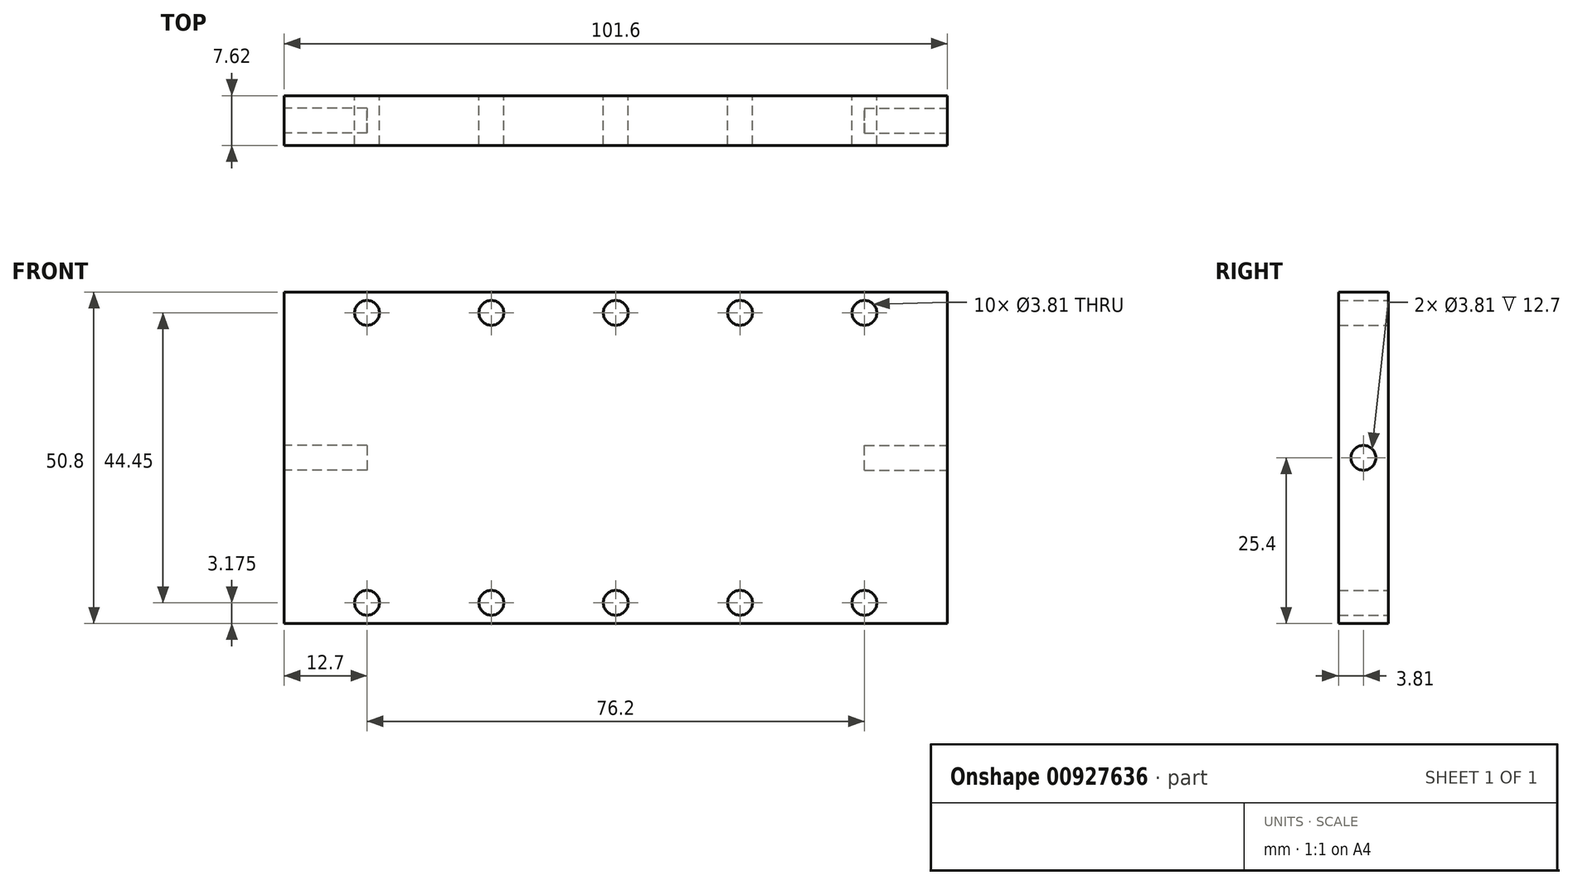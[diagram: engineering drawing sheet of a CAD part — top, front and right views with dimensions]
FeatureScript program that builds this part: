
annotation { "Feature Type Name" : "Feature", "Feature Type Description" : "" }
export const myFeature = defineFeature(function(context is Context, id is Id, definition is map)
    precondition{}
    {
        {
            var Q0;
            Q0=qCreatedBy(makeId("Front.planeOp"),FACE);
            var sketch = newSketch(context, id + "F0", { "sketchPlane" : qUnion([Q0])});
            skLineSegment(sketch, "E0.bottom", {"start": v(-50.8, 25.4) * mm, "end": v(50.8, 25.4) * mm});
            skLineSegment(sketch, "E0.top", {"start": v(-50.8, -25.4) * mm, "end": v(50.8, -25.4) * mm});
            skLineSegment(sketch, "E0.left", {"start": v(-50.8, 25.4) * mm, "end": v(-50.8, -25.4) * mm});
            skLineSegment(sketch, "E0.right", {"start": v(50.8, 25.4) * mm, "end": v(50.8, -25.4) * mm});
            skPoint(sketch, "E0.middle", {"position": v(0, 0) * mm});
            skCircle(sketch, "E1", {"center": v(-38.1, 22.23) * mm, "radius": 1.9 * mm});
            skCircle(sketch, "E2.1.0.0", {"center": v(-19.05, 22.23) * mm, "radius": 1.9 * mm});
            skCircle(sketch, "E2.2.0.0", {"center": v(0, 22.23) * mm, "radius": 1.9 * mm});
            skCircle(sketch, "E2.3.0.0", {"center": v(19.05, 22.23) * mm, "radius": 1.9 * mm});
            skCircle(sketch, "E2.4.0.0", {"center": v(38.1, 22.23) * mm, "radius": 1.9 * mm});
            skLineSegment(sketch, "E2.direction1", {"start": v(-38.1, 22.23) * mm, "end": v(-19.05, 22.23) * mm, "construction": true});
            skCircle(sketch, "E3.MirrorC", {"center": v(-38.1, -22.23) * mm, "radius": 1.9 * mm});
            skCircle(sketch, "E4.MirrorC", {"center": v(-19.05, -22.23) * mm, "radius": 1.9 * mm});
            skCircle(sketch, "E5.MirrorC", {"center": v(19.05, -22.23) * mm, "radius": 1.9 * mm});
            skCircle(sketch, "E6.MirrorC", {"center": v(38.1, -22.23) * mm, "radius": 1.9 * mm});
            skCircle(sketch, "E7.MirrorC", {"center": v(0, -22.23) * mm, "radius": 1.9 * mm});
            skSolve(sketch);
        }
        {
            var Q0;
            Q0=makeQuery(id+"F0.imprint","IMPRINT",FACE,{"disambiguationData":[TD([[makeQuery(id+"F0.imprint","IMPRINT",EDGE,{"derivedFrom":sQuery(id+"F0.wireOp",EDGE,"E0.bottom")}),-1.0]])]});
            extrude(context, id + "F1", {"entities" : qUnion([Q0]), "endBound" : BoundingType.SYMMETRIC, "depth" : 7.62 * mm, "offsetDistance" : 25.4 * mm});
        }
        {
            var Q0;
            Q0=makeQuery(id+"F1.opExtrude","SWEPT_FACE",FACE,{"disambiguationData":[OSD([sQuery(id+"F0.wireOp",EDGE,"E0.right")])]});
            cPlane(context, id + "F2", {"entities" : qUnion([Q0]), "cplaneType" : CPlaneType.OFFSET, "offset" : 0 * mm, "width" : 152.4 * mm, "height" : 152.4 * mm});
        }
        {
            var Q0;
            Q0=qCreatedBy(id+"F2.planeOp",FACE);
            var sketch = newSketch(context, id + "F3", { "sketchPlane" : qUnion([Q0])});
            skCircle(sketch, "E8", {"center": v(0, 0) * mm, "radius": 1.9 * mm});
            skLineSegment(sketch, "E9.bottom", {"start": v(3.81, -25.4) * mm, "end": v(-3.8, -25.4) * mm});
            skLineSegment(sketch, "E9.top", {"start": v(3.8, 25.4) * mm, "end": v(-3.81, 25.4) * mm});
            skLineSegment(sketch, "E9.left", {"start": v(3.81, -25.4) * mm, "end": v(3.8, 25.4) * mm});
            skLineSegment(sketch, "E9.right", {"start": v(-3.8, -25.4) * mm, "end": v(-3.81, 25.4) * mm});
            skSolve(sketch);
        }
        {
            var Q0;
            Q0=makeQuery(id+"F3.imprint","IMPRINT",FACE,{"disambiguationData":[TD([[makeQuery(id+"F3.imprint","IMPRINT",EDGE,{"derivedFrom":sQuery(id+"F3.wireOp",EDGE,"E8")}),1.0]])]});
            extrude(context, id + "F4", {"entities" : qUnion([Q0]), "operationType" : NewBodyOperationType.REMOVE, "oppositeDirection" : true, "depth" : 12.7 * mm, "offsetDistance" : 25.4 * mm});
        }
        {
            var Q0;
            Q0=makeQuery(id+"F1.opExtrude","SWEPT_FACE",FACE,{"disambiguationData":[OSD([sQuery(id+"F0.wireOp",EDGE,"E0.left")])]});
            cPlane(context, id + "F5", {"entities" : qUnion([Q0]), "cplaneType" : CPlaneType.OFFSET, "offset" : 0 * mm, "width" : 152.4 * mm, "height" : 152.4 * mm});
        }
        {
            var Q0;
            Q0=qCreatedBy(id+"F5.planeOp",FACE);
            var sketch = newSketch(context, id + "F6", { "sketchPlane" : qUnion([Q0])});
            skCircle(sketch, "E10", {"center": v(0, 0) * mm, "radius": 1.9 * mm});
            skLineSegment(sketch, "E11.bottom", {"start": v(3.8, 25.4) * mm, "end": v(-3.81, 25.4) * mm});
            skLineSegment(sketch, "E11.top", {"start": v(3.81, -25.4) * mm, "end": v(-3.8, -25.4) * mm});
            skLineSegment(sketch, "E11.left", {"start": v(3.8, 25.4) * mm, "end": v(3.81, -25.4) * mm});
            skLineSegment(sketch, "E11.right", {"start": v(-3.81, 25.4) * mm, "end": v(-3.8, -25.4) * mm});
            skSolve(sketch);
        }
        {
            var Q0;
            Q0=makeQuery(id+"F6.imprint","IMPRINT",FACE,{"disambiguationData":[TD([[makeQuery(id+"F6.imprint","IMPRINT",EDGE,{"derivedFrom":sQuery(id+"F6.wireOp",EDGE,"E10")}),1.0]])]});
            extrude(context, id + "F7", {"entities" : qUnion([Q0]), "operationType" : NewBodyOperationType.REMOVE, "oppositeDirection" : true, "depth" : 12.7 * mm, "offsetDistance" : 25.4 * mm});
        }
    });
